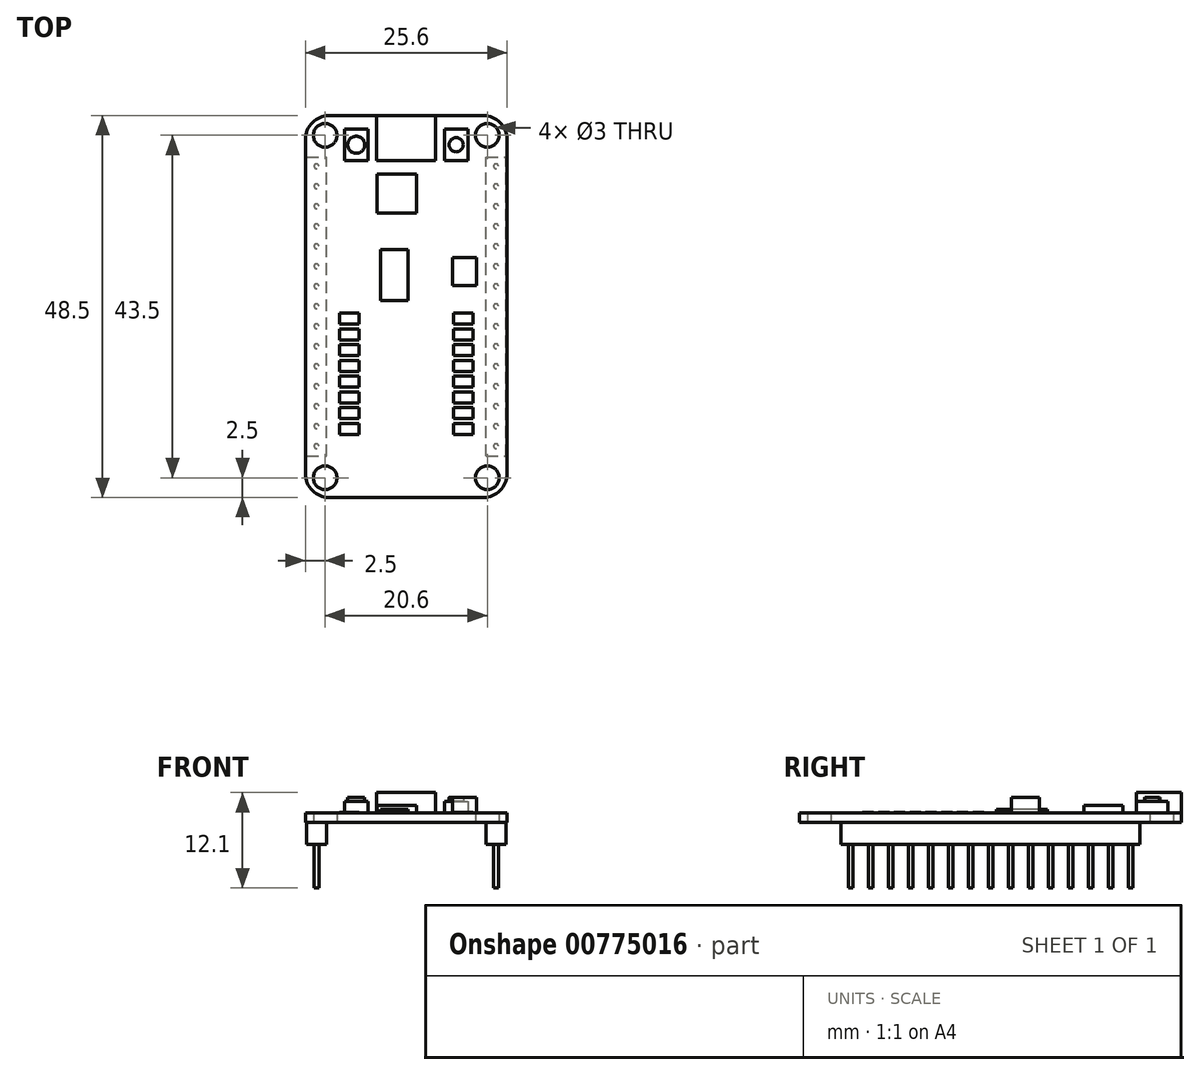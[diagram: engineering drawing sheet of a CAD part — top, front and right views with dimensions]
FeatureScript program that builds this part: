
annotation { "Feature Type Name" : "Feature", "Feature Type Description" : "" }
export const myFeature = defineFeature(function(context is Context, id is Id, definition is map)
    precondition{}
    {
        {
            var Q0;
            Q0=qCreatedBy(makeId("Top.planeOp"),FACE);
            var sketch = newSketch(context, id + "F0", { "sketchPlane" : qUnion([Q0])});
            skLineSegment(sketch, "E0.bottom", {"start": v(-9.8, 24.25) * mm, "end": v(9.8, 24.25) * mm});
            skLineSegment(sketch, "E0.top", {"start": v(-9.8, -24.25) * mm, "end": v(9.8, -24.25) * mm});
            skLineSegment(sketch, "E0.left", {"start": v(-12.8, 21.25) * mm, "end": v(-12.8, -21.25) * mm});
            skLineSegment(sketch, "E0.right", {"start": v(12.8, 21.25) * mm, "end": v(12.8, -21.25) * mm});
            skCircle(sketch, "E1", {"center": v(-10.3, 21.75) * mm, "radius": 1.5 * mm});
            skCircle(sketch, "E2", {"center": v(10.3, 21.75) * mm, "radius": 1.5 * mm});
            skCircle(sketch, "E3", {"center": v(-10.3, -21.75) * mm, "radius": 1.5 * mm});
            skCircle(sketch, "E4", {"center": v(10.3, -21.75) * mm, "radius": 1.5 * mm});
            skPoint(sketch, "E5.visualSharp", {"position": v(-12.8, 24.25) * mm});
            skArc(sketch, "E5.filletArc", {"start": v(-9.8, 24.25) * mm, "mid": v(-11.92, 23.37) * mm, "end": v(-12.8, 21.25) * mm});
            skPoint(sketch, "E6.visualSharp", {"position": v(12.8, 24.25) * mm});
            skArc(sketch, "E6.filletArc", {"start": v(12.8, 21.25) * mm, "mid": v(11.92, 23.37) * mm, "end": v(9.8, 24.25) * mm});
            skPoint(sketch, "E7.visualSharp", {"position": v(12.8, -24.25) * mm});
            skArc(sketch, "E7.filletArc", {"start": v(9.8, -24.25) * mm, "mid": v(11.92, -23.37) * mm, "end": v(12.8, -21.25) * mm});
            skPoint(sketch, "E8.visualSharp", {"position": v(-12.8, -24.25) * mm});
            skArc(sketch, "E8.filletArc", {"start": v(-12.8, -21.25) * mm, "mid": v(-11.92, -23.37) * mm, "end": v(-9.8, -24.25) * mm});
            skSolve(sketch);
        }
        {
            var Q0;
            Q0=makeQuery(id+"F0.imprint","IMPRINT",FACE,{"disambiguationData":[TD([[makeQuery(id+"F0.imprint","IMPRINT",EDGE,{"derivedFrom":sQuery(id+"F0.wireOp",EDGE,"E0.bottom")}),-1.0]])]});
            extrude(context, id + "F1", {"entities" : qUnion([Q0]), "depth" : 1.2 * mm, "offsetDistance" : 25 * mm});
        }
        {
            var Q0;
            Q0=makeQuery(id+"F1.opExtrude","CAP_FACE",FACE,{"disambiguationData":[OSD([sQuery(id+"F0.wireOp",EDGE,"E0.bottom"),sQuery(id+"F0.wireOp",EDGE,"E0.top"),sQuery(id+"F0.wireOp",EDGE,"E0.left"),sQuery(id+"F0.wireOp",EDGE,"E0.right"),sQuery(id+"F0.wireOp",EDGE,"E1"),sQuery(id+"F0.wireOp",EDGE,"E2"),sQuery(id+"F0.wireOp",EDGE,"E3"),sQuery(id+"F0.wireOp",EDGE,"E4"),sQuery(id+"F0.wireOp",EDGE,"E5.filletArc"),sQuery(id+"F0.wireOp",EDGE,"E6.filletArc"),sQuery(id+"F0.wireOp",EDGE,"E7.filletArc"),sQuery(id+"F0.wireOp",EDGE,"E8.filletArc")])],"isStart":true});
            var sketch = newSketch(context, id + "F2", { "sketchPlane" : qUnion([Q0])});
            skLineSegment(sketch, "E9.bottom", {"start": v(-12.65, 19) * mm, "end": v(-10.15, 19) * mm});
            skLineSegment(sketch, "E9.top", {"start": v(-12.65, -19) * mm, "end": v(-10.15, -19) * mm});
            skLineSegment(sketch, "E9.left", {"start": v(-12.65, 19) * mm, "end": v(-12.65, -19) * mm});
            skLineSegment(sketch, "E9.right", {"start": v(-10.15, 19) * mm, "end": v(-10.15, -19) * mm});
            skLineSegment(sketch, "E10.bottom", {"start": v(10.15, 19) * mm, "end": v(12.65, 19) * mm});
            skLineSegment(sketch, "E10.top", {"start": v(10.15, -19) * mm, "end": v(12.65, -19) * mm});
            skLineSegment(sketch, "E10.left", {"start": v(10.15, 19) * mm, "end": v(10.15, -19) * mm});
            skLineSegment(sketch, "E10.right", {"start": v(12.65, 19) * mm, "end": v(12.65, -19) * mm});
            skSolve(sketch);
        }
        {
            var Q0;
            Q0=makeQuery(id+"F2.imprint","IMPRINT",FACE,{"disambiguationData":[TD([[makeQuery(id+"F2.imprint","IMPRINT",EDGE,{"derivedFrom":sQuery(id+"F2.wireOp",EDGE,"E10.bottom")}),-1.0]])]});
            var Q1;
            Q1=makeQuery(id+"F2.imprint","IMPRINT",FACE,{"disambiguationData":[TD([[makeQuery(id+"F2.imprint","IMPRINT",EDGE,{"derivedFrom":sQuery(id+"F2.wireOp",EDGE,"E9.bottom")}),-1.0]])]});
            extrude(context, id + "F3", {"entities" : qUnion([Q0, Q1]), "depth" : 2.8 * mm, "offsetDistance" : 25 * mm});
        }
        {
            var Q0;
            Q0=makeQuery(id+"F3.opExtrude","CAP_FACE",FACE,{"disambiguationData":[OSD([sQuery(id+"F2.wireOp",EDGE,"E9.bottom"),sQuery(id+"F2.wireOp",EDGE,"E9.top"),sQuery(id+"F2.wireOp",EDGE,"E9.left"),sQuery(id+"F2.wireOp",EDGE,"E9.right")])],"isStart":false});
            var sketch = newSketch(context, id + "F4", { "sketchPlane" : qUnion([Q0])});
            skCircle(sketch, "E11", {"center": v(-11.4, 17.73) * mm, "radius": 0.3 * mm});
            skCircle(sketch, "E12.1.0.0", {"center": v(-11.4, 15.2) * mm, "radius": 0.3 * mm});
            skCircle(sketch, "E12.2.0.0", {"center": v(-11.4, 12.65) * mm, "radius": 0.3 * mm});
            skCircle(sketch, "E12.3.0.0", {"center": v(-11.4, 10.11) * mm, "radius": 0.3 * mm});
            skCircle(sketch, "E12.4.0.0", {"center": v(-11.4, 7.57) * mm, "radius": 0.3 * mm});
            skCircle(sketch, "E12.5.0.0", {"center": v(-11.4, 5.03) * mm, "radius": 0.3 * mm});
            skCircle(sketch, "E12.6.0.0", {"center": v(-11.4, 2.5) * mm, "radius": 0.3 * mm});
            skCircle(sketch, "E12.7.0.0", {"center": v(-11.4, -0.05) * mm, "radius": 0.3 * mm});
            skCircle(sketch, "E12.8.0.0", {"center": v(-11.4, -2.59) * mm, "radius": 0.3 * mm});
            skCircle(sketch, "E12.9.0.0", {"center": v(-11.4, -5.13) * mm, "radius": 0.3 * mm});
            skCircle(sketch, "E12.10.0.0", {"center": v(-11.4, -7.67) * mm, "radius": 0.3 * mm});
            skCircle(sketch, "E12.11.0.0", {"center": v(-11.4, -10.2) * mm, "radius": 0.3 * mm});
            skCircle(sketch, "E12.12.0.0", {"center": v(-11.4, -12.75) * mm, "radius": 0.3 * mm});
            skCircle(sketch, "E12.13.0.0", {"center": v(-11.4, -15.29) * mm, "radius": 0.3 * mm});
            skCircle(sketch, "E12.14.0.0", {"center": v(-11.4, -17.83) * mm, "radius": 0.3 * mm});
            skLineSegment(sketch, "E12.direction1", {"start": v(-11.4, 17.73) * mm, "end": v(-11.4, 15.2) * mm, "construction": true});
            skCircle(sketch, "E13", {"center": v(11.4, 17.73) * mm, "radius": 0.3 * mm});
            skCircle(sketch, "E14.1.0.0", {"center": v(11.4, 15.2) * mm, "radius": 0.3 * mm});
            skCircle(sketch, "E14.2.0.0", {"center": v(11.4, 12.65) * mm, "radius": 0.3 * mm});
            skCircle(sketch, "E14.3.0.0", {"center": v(11.4, 10.11) * mm, "radius": 0.3 * mm});
            skCircle(sketch, "E14.4.0.0", {"center": v(11.4, 7.57) * mm, "radius": 0.3 * mm});
            skCircle(sketch, "E14.5.0.0", {"center": v(11.4, 5.03) * mm, "radius": 0.3 * mm});
            skCircle(sketch, "E14.6.0.0", {"center": v(11.4, 2.5) * mm, "radius": 0.3 * mm});
            skCircle(sketch, "E14.7.0.0", {"center": v(11.4, -0.05) * mm, "radius": 0.3 * mm});
            skCircle(sketch, "E14.8.0.0", {"center": v(11.4, -2.59) * mm, "radius": 0.3 * mm});
            skCircle(sketch, "E14.9.0.0", {"center": v(11.4, -5.13) * mm, "radius": 0.3 * mm});
            skCircle(sketch, "E14.10.0.0", {"center": v(11.4, -7.67) * mm, "radius": 0.3 * mm});
            skCircle(sketch, "E14.11.0.0", {"center": v(11.4, -10.2) * mm, "radius": 0.3 * mm});
            skCircle(sketch, "E14.12.0.0", {"center": v(11.4, -12.75) * mm, "radius": 0.3 * mm});
            skCircle(sketch, "E14.13.0.0", {"center": v(11.4, -15.29) * mm, "radius": 0.3 * mm});
            skCircle(sketch, "E14.14.0.0", {"center": v(11.4, -17.83) * mm, "radius": 0.3 * mm});
            skLineSegment(sketch, "E14.direction1", {"start": v(11.4, 17.73) * mm, "end": v(11.4, 15.2) * mm, "construction": true});
            skSolve(sketch);
        }
        {
            var Q0;
            Q0=makeQuery(id+"F4.imprint","IMPRINT",FACE,{"disambiguationData":[TD([[makeQuery(id+"F4.imprint","IMPRINT",EDGE,{"derivedFrom":sQuery(id+"F4.wireOp",EDGE,"E11")}),1.0]])]});
            var Q1;
            Q1=makeQuery(id+"F4.imprint","IMPRINT",FACE,{"disambiguationData":[TD([[makeQuery(id+"F4.imprint","IMPRINT",EDGE,{"derivedFrom":sQuery(id+"F4.wireOp",EDGE,"E12.1.0.0")}),1.0]])]});
            var Q2;
            Q2=makeQuery(id+"F4.imprint","IMPRINT",FACE,{"disambiguationData":[TD([[makeQuery(id+"F4.imprint","IMPRINT",EDGE,{"derivedFrom":sQuery(id+"F4.wireOp",EDGE,"E12.2.0.0")}),1.0]])]});
            var Q3;
            Q3=makeQuery(id+"F4.imprint","IMPRINT",FACE,{"disambiguationData":[TD([[makeQuery(id+"F4.imprint","IMPRINT",EDGE,{"derivedFrom":sQuery(id+"F4.wireOp",EDGE,"E12.3.0.0")}),1.0]])]});
            var Q4;
            Q4=makeQuery(id+"F4.imprint","IMPRINT",FACE,{"disambiguationData":[TD([[makeQuery(id+"F4.imprint","IMPRINT",EDGE,{"derivedFrom":sQuery(id+"F4.wireOp",EDGE,"E12.4.0.0")}),1.0]])]});
            var Q5;
            Q5=makeQuery(id+"F4.imprint","IMPRINT",FACE,{"disambiguationData":[TD([[makeQuery(id+"F4.imprint","IMPRINT",EDGE,{"derivedFrom":sQuery(id+"F4.wireOp",EDGE,"E12.5.0.0")}),1.0]])]});
            var Q6;
            Q6=makeQuery(id+"F4.imprint","IMPRINT",FACE,{"disambiguationData":[TD([[makeQuery(id+"F4.imprint","IMPRINT",EDGE,{"derivedFrom":sQuery(id+"F4.wireOp",EDGE,"E13")}),1.0]])]});
            var Q7;
            Q7=makeQuery(id+"F4.imprint","IMPRINT",FACE,{"disambiguationData":[TD([[makeQuery(id+"F4.imprint","IMPRINT",EDGE,{"derivedFrom":sQuery(id+"F4.wireOp",EDGE,"E14.1.0.0")}),1.0]])]});
            var Q8;
            Q8=makeQuery(id+"F4.imprint","IMPRINT",FACE,{"disambiguationData":[TD([[makeQuery(id+"F4.imprint","IMPRINT",EDGE,{"derivedFrom":sQuery(id+"F4.wireOp",EDGE,"E14.2.0.0")}),1.0]])]});
            var Q9;
            Q9=makeQuery(id+"F4.imprint","IMPRINT",FACE,{"disambiguationData":[TD([[makeQuery(id+"F4.imprint","IMPRINT",EDGE,{"derivedFrom":sQuery(id+"F4.wireOp",EDGE,"E14.3.0.0")}),1.0]])]});
            var Q10;
            Q10=makeQuery(id+"F4.imprint","IMPRINT",FACE,{"disambiguationData":[TD([[makeQuery(id+"F4.imprint","IMPRINT",EDGE,{"derivedFrom":sQuery(id+"F4.wireOp",EDGE,"E14.4.0.0")}),1.0]])]});
            var Q11;
            Q11=makeQuery(id+"F4.imprint","IMPRINT",FACE,{"disambiguationData":[TD([[makeQuery(id+"F4.imprint","IMPRINT",EDGE,{"derivedFrom":sQuery(id+"F4.wireOp",EDGE,"E14.5.0.0")}),1.0]])]});
            var Q12;
            Q12=makeQuery(id+"F4.imprint","IMPRINT",FACE,{"disambiguationData":[TD([[makeQuery(id+"F4.imprint","IMPRINT",EDGE,{"derivedFrom":sQuery(id+"F4.wireOp",EDGE,"E14.6.0.0")}),1.0]])]});
            var Q13;
            Q13=makeQuery(id+"F4.imprint","IMPRINT",FACE,{"disambiguationData":[TD([[makeQuery(id+"F4.imprint","IMPRINT",EDGE,{"derivedFrom":sQuery(id+"F4.wireOp",EDGE,"E14.7.0.0")}),1.0]])]});
            var Q14;
            Q14=makeQuery(id+"F4.imprint","IMPRINT",FACE,{"disambiguationData":[TD([[makeQuery(id+"F4.imprint","IMPRINT",EDGE,{"derivedFrom":sQuery(id+"F4.wireOp",EDGE,"E12.6.0.0")}),1.0]])]});
            var Q15;
            Q15=makeQuery(id+"F4.imprint","IMPRINT",FACE,{"disambiguationData":[TD([[makeQuery(id+"F4.imprint","IMPRINT",EDGE,{"derivedFrom":sQuery(id+"F4.wireOp",EDGE,"E12.7.0.0")}),1.0]])]});
            var Q16;
            Q16=makeQuery(id+"F4.imprint","IMPRINT",FACE,{"disambiguationData":[TD([[makeQuery(id+"F4.imprint","IMPRINT",EDGE,{"derivedFrom":sQuery(id+"F4.wireOp",EDGE,"E12.8.0.0")}),1.0]])]});
            var Q17;
            Q17=makeQuery(id+"F4.imprint","IMPRINT",FACE,{"disambiguationData":[TD([[makeQuery(id+"F4.imprint","IMPRINT",EDGE,{"derivedFrom":sQuery(id+"F4.wireOp",EDGE,"E12.9.0.0")}),1.0]])]});
            var Q18;
            Q18=makeQuery(id+"F4.imprint","IMPRINT",FACE,{"disambiguationData":[TD([[makeQuery(id+"F4.imprint","IMPRINT",EDGE,{"derivedFrom":sQuery(id+"F4.wireOp",EDGE,"E12.10.0.0")}),1.0]])]});
            var Q19;
            Q19=makeQuery(id+"F4.imprint","IMPRINT",FACE,{"disambiguationData":[TD([[makeQuery(id+"F4.imprint","IMPRINT",EDGE,{"derivedFrom":sQuery(id+"F4.wireOp",EDGE,"E12.11.0.0")}),1.0]])]});
            var Q20;
            Q20=makeQuery(id+"F4.imprint","IMPRINT",FACE,{"disambiguationData":[TD([[makeQuery(id+"F4.imprint","IMPRINT",EDGE,{"derivedFrom":sQuery(id+"F4.wireOp",EDGE,"E12.12.0.0")}),1.0]])]});
            var Q21;
            Q21=makeQuery(id+"F4.imprint","IMPRINT",FACE,{"disambiguationData":[TD([[makeQuery(id+"F4.imprint","IMPRINT",EDGE,{"derivedFrom":sQuery(id+"F4.wireOp",EDGE,"E14.8.0.0")}),1.0]])]});
            var Q22;
            Q22=makeQuery(id+"F4.imprint","IMPRINT",FACE,{"disambiguationData":[TD([[makeQuery(id+"F4.imprint","IMPRINT",EDGE,{"derivedFrom":sQuery(id+"F4.wireOp",EDGE,"E14.9.0.0")}),1.0]])]});
            var Q23;
            Q23=makeQuery(id+"F4.imprint","IMPRINT",FACE,{"disambiguationData":[TD([[makeQuery(id+"F4.imprint","IMPRINT",EDGE,{"derivedFrom":sQuery(id+"F4.wireOp",EDGE,"E14.10.0.0")}),1.0]])]});
            var Q24;
            Q24=makeQuery(id+"F4.imprint","IMPRINT",FACE,{"disambiguationData":[TD([[makeQuery(id+"F4.imprint","IMPRINT",EDGE,{"derivedFrom":sQuery(id+"F4.wireOp",EDGE,"E14.11.0.0")}),1.0]])]});
            var Q25;
            Q25=makeQuery(id+"F4.imprint","IMPRINT",FACE,{"disambiguationData":[TD([[makeQuery(id+"F4.imprint","IMPRINT",EDGE,{"derivedFrom":sQuery(id+"F4.wireOp",EDGE,"E14.12.0.0")}),1.0]])]});
            var Q26;
            Q26=makeQuery(id+"F4.imprint","IMPRINT",FACE,{"disambiguationData":[TD([[makeQuery(id+"F4.imprint","IMPRINT",EDGE,{"derivedFrom":sQuery(id+"F4.wireOp",EDGE,"E14.13.0.0")}),1.0]])]});
            var Q27;
            Q27=makeQuery(id+"F4.imprint","IMPRINT",FACE,{"disambiguationData":[TD([[makeQuery(id+"F4.imprint","IMPRINT",EDGE,{"derivedFrom":sQuery(id+"F4.wireOp",EDGE,"E14.14.0.0")}),1.0]])]});
            var Q28;
            Q28=makeQuery(id+"F4.imprint","IMPRINT",FACE,{"disambiguationData":[TD([[makeQuery(id+"F4.imprint","IMPRINT",EDGE,{"derivedFrom":sQuery(id+"F4.wireOp",EDGE,"E12.14.0.0")}),1.0]])]});
            var Q29;
            Q29=makeQuery(id+"F4.imprint","IMPRINT",FACE,{"disambiguationData":[TD([[makeQuery(id+"F4.imprint","IMPRINT",EDGE,{"derivedFrom":sQuery(id+"F4.wireOp",EDGE,"E12.13.0.0")}),1.0]])]});
            extrude(context, id + "F5", {"entities" : qUnion([Q0, Q1, Q2, Q3, Q4, Q5, Q6, Q7, Q8, Q9, Q10, Q11, Q12, Q13, Q14, Q15, Q16, Q17, Q18, Q19, Q20, Q21, Q22, Q23, Q24, Q25, Q26, Q27, Q28, Q29]), "operationType" : NewBodyOperationType.ADD, "depth" : 5.5 * mm, "offsetDistance" : 25 * mm});
        }
        {
            var Q0;
            Q0=makeQuery(id+"F1.opExtrude","CAP_FACE",FACE,{"disambiguationData":[OSD([sQuery(id+"F0.wireOp",EDGE,"E0.bottom"),sQuery(id+"F0.wireOp",EDGE,"E0.top"),sQuery(id+"F0.wireOp",EDGE,"E0.left"),sQuery(id+"F0.wireOp",EDGE,"E0.right"),sQuery(id+"F0.wireOp",EDGE,"E1"),sQuery(id+"F0.wireOp",EDGE,"E2"),sQuery(id+"F0.wireOp",EDGE,"E3"),sQuery(id+"F0.wireOp",EDGE,"E4"),sQuery(id+"F0.wireOp",EDGE,"E5.filletArc"),sQuery(id+"F0.wireOp",EDGE,"E6.filletArc"),sQuery(id+"F0.wireOp",EDGE,"E7.filletArc"),sQuery(id+"F0.wireOp",EDGE,"E8.filletArc")])],"isStart":false});
            var sketch = newSketch(context, id + "F6", { "sketchPlane" : qUnion([Q0])});
            skLineSegment(sketch, "E15.bottom", {"start": v(-3.75, 24.25) * mm, "end": v(3.75, 24.25) * mm});
            skLineSegment(sketch, "E15.top", {"start": v(-3.75, 18.55) * mm, "end": v(3.75, 18.55) * mm});
            skLineSegment(sketch, "E15.left", {"start": v(-3.75, 24.25) * mm, "end": v(-3.75, 18.55) * mm});
            skLineSegment(sketch, "E15.right", {"start": v(3.75, 24.25) * mm, "end": v(3.75, 18.55) * mm});
            skSolve(sketch);
        }
        {
            var Q0;
            Q0=makeQuery(id+"F1.opExtrude","CAP_FACE",FACE,{"disambiguationData":[OSD([sQuery(id+"F0.wireOp",EDGE,"E0.bottom"),sQuery(id+"F0.wireOp",EDGE,"E0.top"),sQuery(id+"F0.wireOp",EDGE,"E0.left"),sQuery(id+"F0.wireOp",EDGE,"E0.right"),sQuery(id+"F0.wireOp",EDGE,"E1"),sQuery(id+"F0.wireOp",EDGE,"E2"),sQuery(id+"F0.wireOp",EDGE,"E3"),sQuery(id+"F0.wireOp",EDGE,"E4"),sQuery(id+"F0.wireOp",EDGE,"E5.filletArc"),sQuery(id+"F0.wireOp",EDGE,"E6.filletArc"),sQuery(id+"F0.wireOp",EDGE,"E7.filletArc"),sQuery(id+"F0.wireOp",EDGE,"E8.filletArc")])],"isStart":false});
            var sketch = newSketch(context, id + "F7", { "sketchPlane" : qUnion([Q0])});
            skLineSegment(sketch, "E16.bottom", {"start": v(-7.85, 22.55) * mm, "end": v(-4.85, 22.55) * mm});
            skLineSegment(sketch, "E16.top", {"start": v(-7.85, 18.55) * mm, "end": v(-4.85, 18.55) * mm});
            skLineSegment(sketch, "E16.left", {"start": v(-7.85, 22.55) * mm, "end": v(-7.85, 18.55) * mm});
            skLineSegment(sketch, "E16.right", {"start": v(-4.85, 22.55) * mm, "end": v(-4.85, 18.55) * mm});
            skLineSegment(sketch, "E17.bottom", {"start": v(4.85, 22.55) * mm, "end": v(7.85, 22.55) * mm});
            skLineSegment(sketch, "E17.top", {"start": v(4.85, 18.55) * mm, "end": v(7.85, 18.55) * mm});
            skLineSegment(sketch, "E17.left", {"start": v(4.85, 22.55) * mm, "end": v(4.85, 18.55) * mm});
            skLineSegment(sketch, "E17.right", {"start": v(7.85, 22.55) * mm, "end": v(7.85, 18.55) * mm});
            skSolve(sketch);
        }
        {
            var Q0;
            Q0 = qSketchRegion(id + "F7", true);
            extrude(context, id + "F8", {"entities" : qUnion([Q0]), "depth" : 1.5 * mm, "offsetDistance" : 25 * mm});
        }
        {
            var Q0;
            Q0=makeQuery(id+"F8.opExtrude","CAP_FACE",FACE,{"disambiguationData":[OSD([sQuery(id+"F7.wireOp",EDGE,"E16.bottom"),sQuery(id+"F7.wireOp",EDGE,"E16.top"),sQuery(id+"F7.wireOp",EDGE,"E16.left"),sQuery(id+"F7.wireOp",EDGE,"E16.right")])],"isStart":false});
            var sketch = newSketch(context, id + "F9", { "sketchPlane" : qUnion([Q0])});
            skCircle(sketch, "E18", {"center": v(-6.35, 20.55) * mm, "radius": 1.09 * mm});
            skCircle(sketch, "E19", {"center": v(6.35, 20.55) * mm, "radius": 0.9 * mm});
            skSolve(sketch);
        }
        {
            var Q0;
            Q0 = qSketchRegion(id + "F9", true);
            extrude(context, id + "F10", {"entities" : qUnion([Q0]), "operationType" : NewBodyOperationType.ADD, "depth" : 0.5 * mm, "offsetDistance" : 25 * mm});
        }
        {
            var Q0;
            Q0=makeQuery(id+"F1.opExtrude","CAP_FACE",FACE,{"disambiguationData":[OSD([sQuery(id+"F0.wireOp",EDGE,"E0.bottom"),sQuery(id+"F0.wireOp",EDGE,"E0.top"),sQuery(id+"F0.wireOp",EDGE,"E0.left"),sQuery(id+"F0.wireOp",EDGE,"E0.right"),sQuery(id+"F0.wireOp",EDGE,"E1"),sQuery(id+"F0.wireOp",EDGE,"E2"),sQuery(id+"F0.wireOp",EDGE,"E3"),sQuery(id+"F0.wireOp",EDGE,"E4"),sQuery(id+"F0.wireOp",EDGE,"E5.filletArc"),sQuery(id+"F0.wireOp",EDGE,"E6.filletArc"),sQuery(id+"F0.wireOp",EDGE,"E7.filletArc"),sQuery(id+"F0.wireOp",EDGE,"E8.filletArc")])],"isStart":false});
            var sketch = newSketch(context, id + "F11", { "sketchPlane" : qUnion([Q0])});
            skLineSegment(sketch, "E20.bottom", {"start": v(-8.5, -14.85) * mm, "end": v(-6, -14.85) * mm});
            skLineSegment(sketch, "E20.top", {"start": v(-8.5, -16.25) * mm, "end": v(-6, -16.25) * mm});
            skLineSegment(sketch, "E20.left", {"start": v(-8.5, -14.85) * mm, "end": v(-8.5, -16.25) * mm});
            skLineSegment(sketch, "E20.right", {"start": v(-6, -14.85) * mm, "end": v(-6, -16.25) * mm});
            skLineSegment(sketch, "E21.1.0.0", {"start": v(-8.5, -14.25) * mm, "end": v(-6, -14.25) * mm});
            skLineSegment(sketch, "E21.1.0.1", {"start": v(-6, -12.85) * mm, "end": v(-6, -14.25) * mm});
            skLineSegment(sketch, "E21.1.0.2", {"start": v(-8.5, -12.85) * mm, "end": v(-6, -12.85) * mm});
            skLineSegment(sketch, "E21.1.0.3", {"start": v(-8.5, -12.85) * mm, "end": v(-8.5, -14.25) * mm});
            skLineSegment(sketch, "E21.2.0.0", {"start": v(-8.5, -12.25) * mm, "end": v(-6, -12.25) * mm});
            skLineSegment(sketch, "E21.2.0.1", {"start": v(-6, -10.85) * mm, "end": v(-6, -12.25) * mm});
            skLineSegment(sketch, "E21.2.0.2", {"start": v(-8.5, -10.85) * mm, "end": v(-6, -10.85) * mm});
            skLineSegment(sketch, "E21.2.0.3", {"start": v(-8.5, -10.85) * mm, "end": v(-8.5, -12.25) * mm});
            skLineSegment(sketch, "E21.3.0.0", {"start": v(-8.5, -10.25) * mm, "end": v(-6, -10.25) * mm});
            skLineSegment(sketch, "E21.3.0.1", {"start": v(-6, -8.85) * mm, "end": v(-6, -10.25) * mm});
            skLineSegment(sketch, "E21.3.0.2", {"start": v(-8.5, -8.85) * mm, "end": v(-6, -8.85) * mm});
            skLineSegment(sketch, "E21.3.0.3", {"start": v(-8.5, -8.85) * mm, "end": v(-8.5, -10.25) * mm});
            skLineSegment(sketch, "E21.4.0.0", {"start": v(-8.5, -8.25) * mm, "end": v(-6, -8.25) * mm});
            skLineSegment(sketch, "E21.4.0.1", {"start": v(-6, -6.85) * mm, "end": v(-6, -8.25) * mm});
            skLineSegment(sketch, "E21.4.0.2", {"start": v(-8.5, -6.85) * mm, "end": v(-6, -6.85) * mm});
            skLineSegment(sketch, "E21.4.0.3", {"start": v(-8.5, -6.85) * mm, "end": v(-8.5, -8.25) * mm});
            skLineSegment(sketch, "E21.5.0.0", {"start": v(-8.5, -6.25) * mm, "end": v(-6, -6.25) * mm});
            skLineSegment(sketch, "E21.5.0.1", {"start": v(-6, -4.85) * mm, "end": v(-6, -6.25) * mm});
            skLineSegment(sketch, "E21.5.0.2", {"start": v(-8.5, -4.85) * mm, "end": v(-6, -4.85) * mm});
            skLineSegment(sketch, "E21.5.0.3", {"start": v(-8.5, -4.85) * mm, "end": v(-8.5, -6.25) * mm});
            skLineSegment(sketch, "E21.6.0.0", {"start": v(-8.5, -4.25) * mm, "end": v(-6, -4.25) * mm});
            skLineSegment(sketch, "E21.6.0.1", {"start": v(-6, -2.85) * mm, "end": v(-6, -4.25) * mm});
            skLineSegment(sketch, "E21.6.0.2", {"start": v(-8.5, -2.85) * mm, "end": v(-6, -2.85) * mm});
            skLineSegment(sketch, "E21.6.0.3", {"start": v(-8.5, -2.85) * mm, "end": v(-8.5, -4.25) * mm});
            skLineSegment(sketch, "E21.7.0.0", {"start": v(-8.5, -2.25) * mm, "end": v(-6, -2.25) * mm});
            skLineSegment(sketch, "E21.7.0.1", {"start": v(-6, -0.85) * mm, "end": v(-6, -2.25) * mm});
            skLineSegment(sketch, "E21.7.0.2", {"start": v(-8.5, -0.85) * mm, "end": v(-6, -0.85) * mm});
            skLineSegment(sketch, "E21.7.0.3", {"start": v(-8.5, -0.85) * mm, "end": v(-8.5, -2.25) * mm});
            skLineSegment(sketch, "E21.direction1", {"start": v(-8.5, -16.25) * mm, "end": v(-8.5, -14.25) * mm, "construction": true});
            skLineSegment(sketch, "E22.bottom", {"start": v(6, -14.85) * mm, "end": v(8.5, -14.85) * mm});
            skLineSegment(sketch, "E22.top", {"start": v(6, -16.25) * mm, "end": v(8.5, -16.25) * mm});
            skLineSegment(sketch, "E22.left", {"start": v(6, -14.85) * mm, "end": v(6, -16.25) * mm});
            skLineSegment(sketch, "E22.right", {"start": v(8.5, -14.85) * mm, "end": v(8.5, -16.25) * mm});
            skLineSegment(sketch, "E23.1.0.0", {"start": v(6, -12.85) * mm, "end": v(8.5, -12.85) * mm});
            skLineSegment(sketch, "E23.1.0.1", {"start": v(6, -12.85) * mm, "end": v(6, -14.25) * mm});
            skLineSegment(sketch, "E23.1.0.2", {"start": v(6, -14.25) * mm, "end": v(8.5, -14.25) * mm});
            skLineSegment(sketch, "E23.1.0.3", {"start": v(8.5, -12.85) * mm, "end": v(8.5, -14.25) * mm});
            skLineSegment(sketch, "E23.2.0.0", {"start": v(6, -10.85) * mm, "end": v(8.5, -10.85) * mm});
            skLineSegment(sketch, "E23.2.0.1", {"start": v(6, -10.85) * mm, "end": v(6, -12.25) * mm});
            skLineSegment(sketch, "E23.2.0.2", {"start": v(6, -12.25) * mm, "end": v(8.5, -12.25) * mm});
            skLineSegment(sketch, "E23.2.0.3", {"start": v(8.5, -10.85) * mm, "end": v(8.5, -12.25) * mm});
            skLineSegment(sketch, "E23.3.0.0", {"start": v(6, -8.85) * mm, "end": v(8.5, -8.85) * mm});
            skLineSegment(sketch, "E23.3.0.1", {"start": v(6, -8.85) * mm, "end": v(6, -10.25) * mm});
            skLineSegment(sketch, "E23.3.0.2", {"start": v(6, -10.25) * mm, "end": v(8.5, -10.25) * mm});
            skLineSegment(sketch, "E23.3.0.3", {"start": v(8.5, -8.85) * mm, "end": v(8.5, -10.25) * mm});
            skLineSegment(sketch, "E23.4.0.0", {"start": v(6, -6.85) * mm, "end": v(8.5, -6.85) * mm});
            skLineSegment(sketch, "E23.4.0.1", {"start": v(6, -6.85) * mm, "end": v(6, -8.25) * mm});
            skLineSegment(sketch, "E23.4.0.2", {"start": v(6, -8.25) * mm, "end": v(8.5, -8.25) * mm});
            skLineSegment(sketch, "E23.4.0.3", {"start": v(8.5, -6.85) * mm, "end": v(8.5, -8.25) * mm});
            skLineSegment(sketch, "E23.5.0.0", {"start": v(6, -4.85) * mm, "end": v(8.5, -4.85) * mm});
            skLineSegment(sketch, "E23.5.0.1", {"start": v(6, -4.85) * mm, "end": v(6, -6.25) * mm});
            skLineSegment(sketch, "E23.5.0.2", {"start": v(6, -6.25) * mm, "end": v(8.5, -6.25) * mm});
            skLineSegment(sketch, "E23.5.0.3", {"start": v(8.5, -4.85) * mm, "end": v(8.5, -6.25) * mm});
            skLineSegment(sketch, "E23.6.0.0", {"start": v(6, -2.85) * mm, "end": v(8.5, -2.85) * mm});
            skLineSegment(sketch, "E23.6.0.1", {"start": v(6, -2.85) * mm, "end": v(6, -4.25) * mm});
            skLineSegment(sketch, "E23.6.0.2", {"start": v(6, -4.25) * mm, "end": v(8.5, -4.25) * mm});
            skLineSegment(sketch, "E23.6.0.3", {"start": v(8.5, -2.85) * mm, "end": v(8.5, -4.25) * mm});
            skLineSegment(sketch, "E23.7.0.0", {"start": v(6, -0.85) * mm, "end": v(8.5, -0.85) * mm});
            skLineSegment(sketch, "E23.7.0.1", {"start": v(6, -0.85) * mm, "end": v(6, -2.25) * mm});
            skLineSegment(sketch, "E23.7.0.2", {"start": v(6, -2.25) * mm, "end": v(8.5, -2.25) * mm});
            skLineSegment(sketch, "E23.7.0.3", {"start": v(8.5, -0.85) * mm, "end": v(8.5, -2.25) * mm});
            skLineSegment(sketch, "E23.direction1", {"start": v(6, -14.85) * mm, "end": v(6, -12.85) * mm, "construction": true});
            skSolve(sketch);
        }
        {
            var Q0;
            Q0 = qSketchRegion(id + "F11", true);
            extrude(context, id + "F12", {"entities" : qUnion([Q0]), "depth" : 0.1 * mm, "offsetDistance" : 25 * mm});
        }
        {
            var Q0;
            Q0 = qSketchRegion(id + "F6", true);
            var Q1;
            Q1 = qSketchRegion(id + "F14", true);
            extrude(context, id + "F13", {"entities" : qUnion([Q0, Q1]), "depth" : 2.6 * mm, "offsetDistance" : 25 * mm});
        }
        {
            var Q0;
            Q0=makeQuery(id+"F1.opExtrude","CAP_FACE",FACE,{"disambiguationData":[OSD([sQuery(id+"F0.wireOp",EDGE,"E0.bottom"),sQuery(id+"F0.wireOp",EDGE,"E0.top"),sQuery(id+"F0.wireOp",EDGE,"E0.left"),sQuery(id+"F0.wireOp",EDGE,"E0.right"),sQuery(id+"F0.wireOp",EDGE,"E1"),sQuery(id+"F0.wireOp",EDGE,"E2"),sQuery(id+"F0.wireOp",EDGE,"E3"),sQuery(id+"F0.wireOp",EDGE,"E4"),sQuery(id+"F0.wireOp",EDGE,"E5.filletArc"),sQuery(id+"F0.wireOp",EDGE,"E6.filletArc"),sQuery(id+"F0.wireOp",EDGE,"E7.filletArc"),sQuery(id+"F0.wireOp",EDGE,"E8.filletArc")])],"isStart":false});
            var sketch = newSketch(context, id + "F14", { "sketchPlane" : qUnion([Q0])});
            skLineSegment(sketch, "E24.bottom", {"start": v(5.9, 2.65) * mm, "end": v(8.9, 2.65) * mm});
            skLineSegment(sketch, "E24.top", {"start": v(5.9, 6.25) * mm, "end": v(8.9, 6.25) * mm});
            skLineSegment(sketch, "E24.left", {"start": v(5.9, 2.65) * mm, "end": v(5.9, 6.25) * mm});
            skLineSegment(sketch, "E24.right", {"start": v(8.9, 2.65) * mm, "end": v(8.9, 6.25) * mm});
            skSolve(sketch);
        }
        {
            var Q0;
            Q0 = qSketchRegion(id + "F14", true);
            extrude(context, id + "F15", {"entities" : qUnion([Q0]), "depth" : 2 * mm, "offsetDistance" : 25 * mm});
        }
        {
            var Q0;
            Q0=qCreatedBy(makeId("Top.planeOp"),FACE);
            var sketch = newSketch(context, id + "F16", { "sketchPlane" : qUnion([Q0])});
            skLineSegment(sketch, "E25.bottom", {"start": v(-3.25, 7.25) * mm, "end": v(0.25, 7.25) * mm});
            skLineSegment(sketch, "E25.top", {"start": v(-3.25, 0.75) * mm, "end": v(0.25, 0.75) * mm});
            skLineSegment(sketch, "E25.left", {"start": v(-3.25, 7.25) * mm, "end": v(-3.25, 0.75) * mm});
            skLineSegment(sketch, "E25.right", {"start": v(0.25, 7.25) * mm, "end": v(0.25, 0.75) * mm});
            skSolve(sketch);
        }
        {
            var Q0;
            Q0 = qSketchRegion(id + "F16", true);
            extrude(context, id + "F17", {"entities" : qUnion([Q0]), "operationType" : NewBodyOperationType.ADD, "depth" : 1.65 * mm, "offsetDistance" : 25 * mm});
        }
        {
            var Q0;
            Q0=makeQuery(id+"F1.opExtrude","CAP_FACE",FACE,{"disambiguationData":[OSD([sQuery(id+"F0.wireOp",EDGE,"E0.bottom"),sQuery(id+"F0.wireOp",EDGE,"E0.top"),sQuery(id+"F0.wireOp",EDGE,"E0.left"),sQuery(id+"F0.wireOp",EDGE,"E0.right"),sQuery(id+"F0.wireOp",EDGE,"E1"),sQuery(id+"F0.wireOp",EDGE,"E2"),sQuery(id+"F0.wireOp",EDGE,"E3"),sQuery(id+"F0.wireOp",EDGE,"E4"),sQuery(id+"F0.wireOp",EDGE,"E5.filletArc"),sQuery(id+"F0.wireOp",EDGE,"E6.filletArc"),sQuery(id+"F0.wireOp",EDGE,"E7.filletArc"),sQuery(id+"F0.wireOp",EDGE,"E8.filletArc")])],"isStart":false});
            var sketch = newSketch(context, id + "F18", { "sketchPlane" : qUnion([Q0])});
            skLineSegment(sketch, "E26.bottom", {"start": v(-3.7, 16.85) * mm, "end": v(1.3, 16.85) * mm});
            skLineSegment(sketch, "E26.top", {"start": v(-3.7, 11.85) * mm, "end": v(1.3, 11.85) * mm});
            skLineSegment(sketch, "E26.left", {"start": v(-3.7, 16.85) * mm, "end": v(-3.7, 11.85) * mm});
            skLineSegment(sketch, "E26.right", {"start": v(1.3, 16.85) * mm, "end": v(1.3, 11.85) * mm});
            skSolve(sketch);
        }
        {
            var Q0;
            Q0 = qSketchRegion(id + "F18", true);
            extrude(context, id + "F19", {"entities" : qUnion([Q0]), "operationType" : NewBodyOperationType.ADD, "depth" : 1 * mm, "offsetDistance" : 25 * mm});
        }
    });
